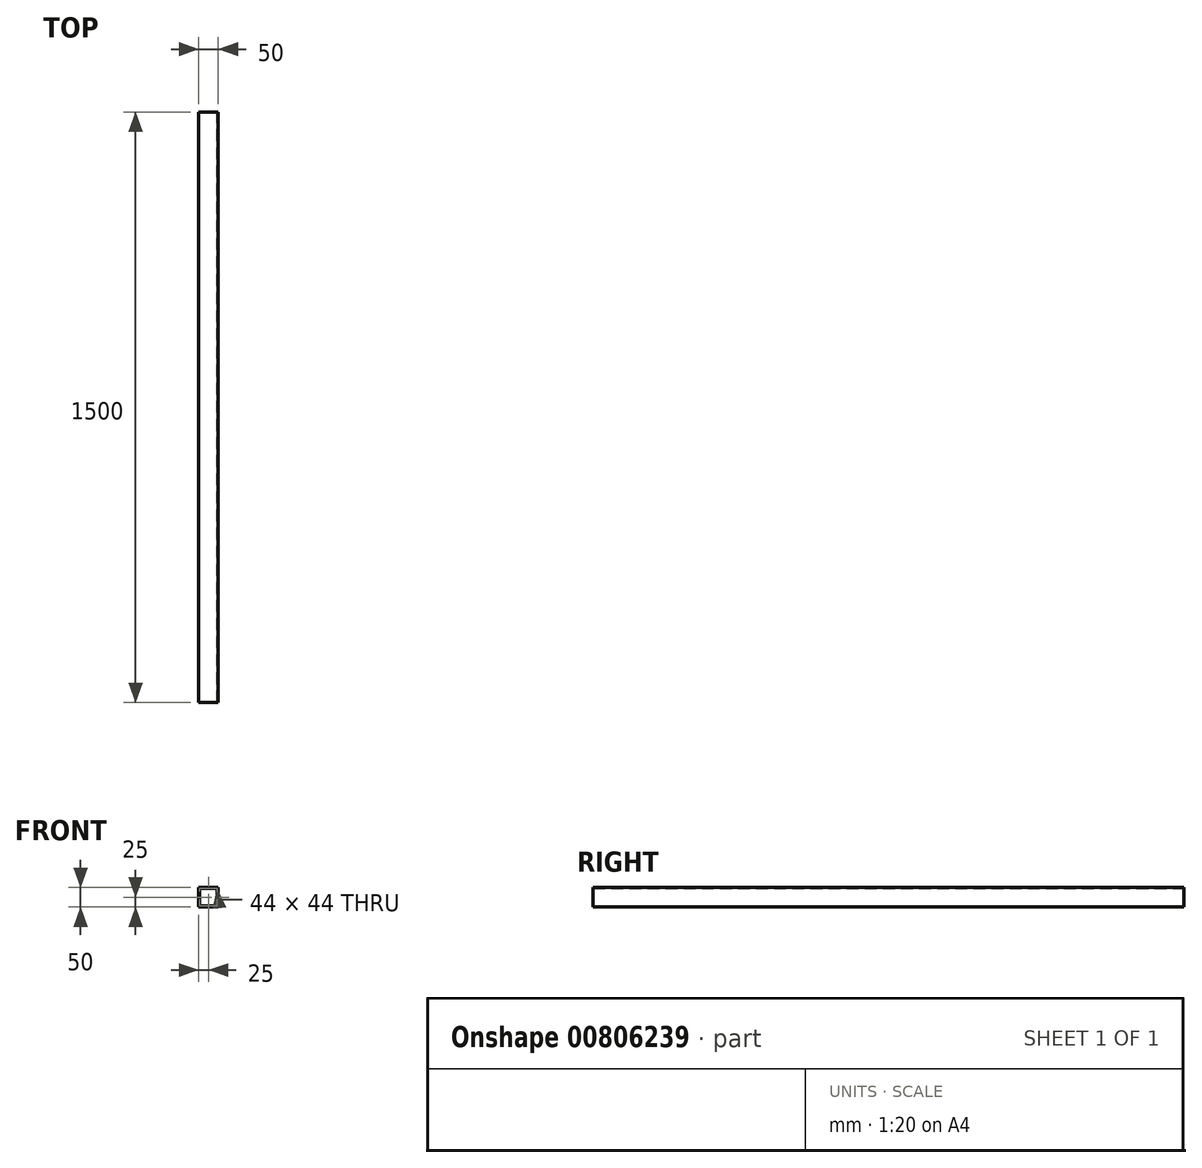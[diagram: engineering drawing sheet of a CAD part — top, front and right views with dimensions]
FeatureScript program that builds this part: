
annotation { "Feature Type Name" : "Feature", "Feature Type Description" : "" }
export const myFeature = defineFeature(function(context is Context, id is Id, definition is map)
    precondition{}
    {
        {
            var Q0;
            Q0=qCreatedBy(makeId("Front.planeOp"),FACE);
            var sketch = newSketch(context, id + "F0", { "sketchPlane" : qUnion([Q0])});
            skLineSegment(sketch, "E0.bottom", {"start": v(25, -25) * mm, "end": v(-25, -25) * mm});
            skLineSegment(sketch, "E0.top", {"start": v(25, 25) * mm, "end": v(-25, 25) * mm});
            skLineSegment(sketch, "E0.left", {"start": v(25, -25) * mm, "end": v(25, 25) * mm});
            skLineSegment(sketch, "E0.right", {"start": v(-25, -25) * mm, "end": v(-25, 25) * mm});
            skPoint(sketch, "E0.middle", {"position": v(0, 0) * mm});
            skLineSegment(sketch, "E1.0", {"start": v(22, 22) * mm, "end": v(-22, 22) * mm});
            skLineSegment(sketch, "E1.1", {"start": v(22, -22) * mm, "end": v(22, 22) * mm});
            skLineSegment(sketch, "E1.2", {"start": v(22, -22) * mm, "end": v(-22, -22) * mm});
            skLineSegment(sketch, "E1.3", {"start": v(-22, -22) * mm, "end": v(-22, 22) * mm});
            skSolve(sketch);
        }
        {
            var Q0;
            Q0=makeQuery(id+"F0.imprint","IMPRINT",FACE,{"disambiguationData":[TD([[makeQuery(id+"F0.imprint","IMPRINT",EDGE,{"derivedFrom":sQuery(id+"F0.wireOp",EDGE,"E0.bottom")}),-1.0]])]});
            extrude(context, id + "F1", {"entities" : qUnion([Q0]), "depth" : 1500 * mm, "offsetDistance" : 25 * mm});
        }
    });
